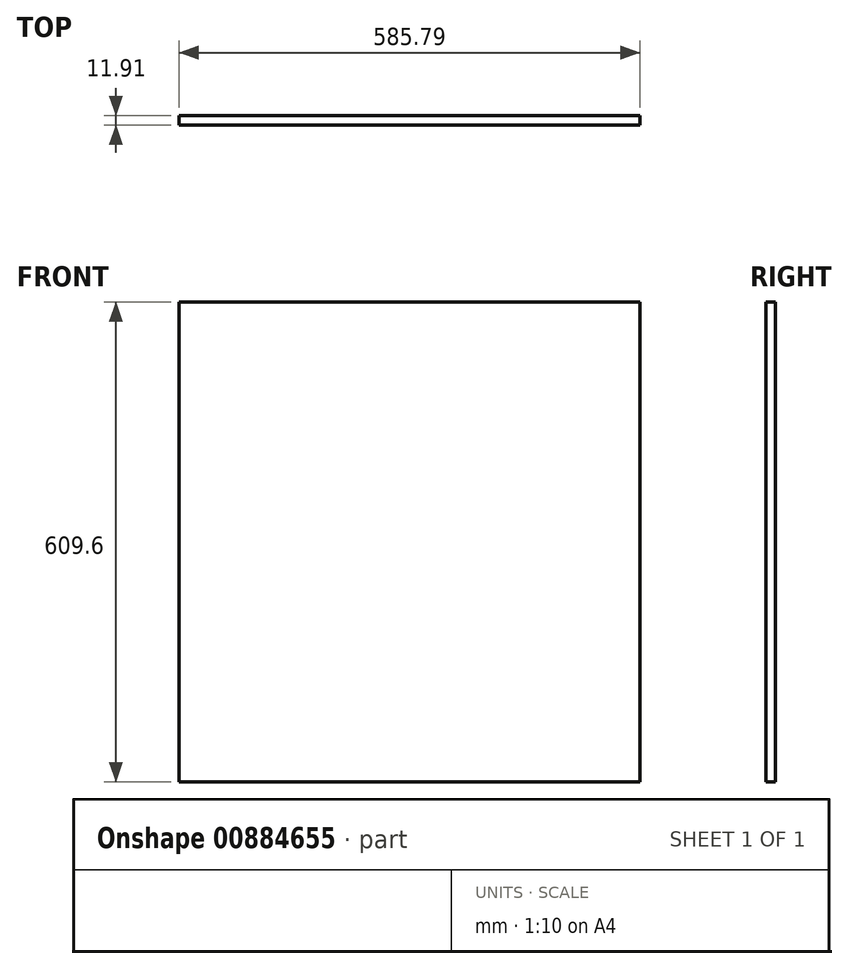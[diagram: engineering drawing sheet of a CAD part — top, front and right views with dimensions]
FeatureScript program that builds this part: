
annotation { "Feature Type Name" : "Feature", "Feature Type Description" : "" }
export const myFeature = defineFeature(function(context is Context, id is Id, definition is map)
    precondition{}
    {
        {
            var Q0;
            Q0=qCreatedBy(makeId("Front.planeOp"),FACE);
            var sketch = newSketch(context, id + "F0", { "sketchPlane" : qUnion([Q0])});
            skLineSegment(sketch, "E0.bottom", {"start": v(-298.45, 381) * mm, "end": v(287.34, 381) * mm});
            skLineSegment(sketch, "E0.top", {"start": v(-298.45, -228.6) * mm, "end": v(287.34, -228.6) * mm});
            skLineSegment(sketch, "E0.left", {"start": v(-298.45, 381) * mm, "end": v(-298.45, -228.6) * mm});
            skLineSegment(sketch, "E0.right", {"start": v(287.34, 381) * mm, "end": v(287.34, -228.6) * mm});
            skSolve(sketch);
        }
        {
            var Q0;
            Q0=makeQuery(id+"F0.imprint","IMPRINT",FACE,{"disambiguationData":[TD([[makeQuery(id+"F0.imprint","IMPRINT",EDGE,{"derivedFrom":sQuery(id+"F0.wireOp",EDGE,"E0.bottom")}),-1.0]])]});
            extrude(context, id + "F1", {"entities" : qUnion([Q0]), "depth" : 11.9 * mm, "offsetDistance" : 25.4 * mm});
        }
    });
